# Revit family: Basin-Zoeller-24x24-912_Series
name_source: partatom
category: Mechanical Equipment
revit_build: Autodesk Revit 2014 (Build: 20130308_1515(x64)
units: mm (PartAtom-declared; Revit-internal decimal feet)

## types (3) — shared parameters
Assembly Code = D2030400
Basin Type = Poly Structural Foam (PSF) w/ alarm
CW Connection = Yes
Default Elevation = 0"
Discharge Size = 2" NPT
HW Connection = No
Hertz = 60
Inlet Radius = 1 3/4"
Insulation = Class B
Manufacturer = Zoeller
Material = Poly Structural Foam (PSF)
Max. Operating Temp. = 130°F (54°C)
Motor Protection = Auto reset thermal overload
Operation = Automatic
Phase = 1
Price = Prices may vary. Please consult Manufacturer Representative for most up-to-date price list.
Product Documentation Link = http://cdn.qleapahead.com
Product Page URL = http://www.zoellerpumps.com
Radius = 12 1/4"
Solid Handling = 2" (50mm) spherical solids
URL = http://www.zoeller.com
Vent Connection = No
Vent Connection Diameter = 2"
Vent Connection Radius = 1"
Voltage = 115 V
Waste Connection = Yes

## per-type parameters (varying)
| type | Amps | Cooling | Cord Length | Description | Diameter | Flow @ 5' | Height | Model | Pump Housing | RPM | Shipping Weight | Type |
| 912-1112 - 115V | 5.5 | Oil Free | 240" | 912 Package Systems. Automatic 211 - Poly Molder Basin w/ 2V2D PSF Simplex Cover. | 25" | 82 GPM | 25 1/2" | 912-1112 | Engineered Plastic | 3400 | 54 lbs. | Permanent split capacitor |
| 912-1114 - 115V | 9.4 | Oil Filled | 180" | 912 Package Systems. Automatic 264 - Poly Molder Basin w/ 2V2D PSF Simplex Cover. | 25" | 90 GPM | 25 1/2" | 912-1114 | Zoeller Powder Coated Cast Iron | 1725 | 75 lbs. | Permanent Split Capacitator |
| 912-1116 - 115V | 10.4 | Oil Filled | 120" | 912 Package Systems. Automatic 266 - Poly Molder Basin w/ 2V2D PSF Simplex Cover. | 18" | 128 GPM | 30" | 912-1116 | Cast Iron | 1725 | 78 lbs. | Split Phase |

## geometry (parser evidence)
native form markers: Sweep x2
no freeform markers — native parametric forms only
